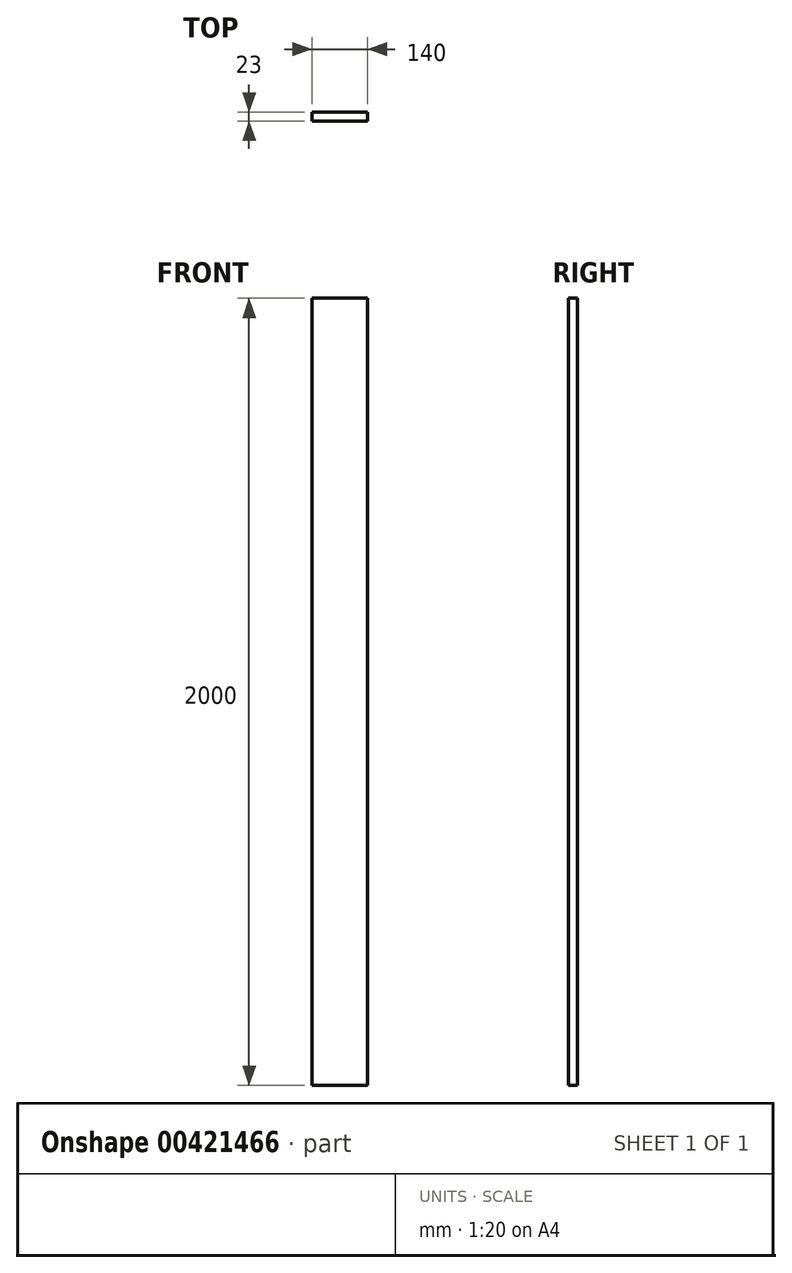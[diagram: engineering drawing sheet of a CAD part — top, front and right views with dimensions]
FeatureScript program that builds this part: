
annotation { "Feature Type Name" : "Feature", "Feature Type Description" : "" }
export const myFeature = defineFeature(function(context is Context, id is Id, definition is map)
    precondition{}
    {
        {
            var Q0;
            Q0=qCreatedBy(makeId("Front.planeOp"),FACE);
            var sketch = newSketch(context, id + "F0", { "sketchPlane" : qUnion([Q0])});
            skLineSegment(sketch, "E0.bottom", {"start": v(-149.18, -984.7) * mm, "end": v(-289.18, -984.7) * mm});
            skLineSegment(sketch, "E0.top", {"start": v(-149.18, 1015.3) * mm, "end": v(-289.18, 1015.3) * mm});
            skLineSegment(sketch, "E0.left", {"start": v(-149.18, -984.7) * mm, "end": v(-149.18, 1015.3) * mm});
            skLineSegment(sketch, "E0.right", {"start": v(-289.18, -984.7) * mm, "end": v(-289.18, 1015.3) * mm});
            skPoint(sketch, "E0.middle", {"position": v(-219.18, 15.3) * mm});
            skSolve(sketch);
        }
        {
            var Q0;
            Q0=makeQuery(id+"F0.imprint","IMPRINT",FACE,{"disambiguationData":[TD([[makeQuery(id+"F0.imprint","IMPRINT",EDGE,{"derivedFrom":sQuery(id+"F0.wireOp",EDGE,"E0.bottom")}),-1.0]])]});
            extrude(context, id + "F1", {"entities" : qUnion([Q0]), "depth" : 23 * mm});
        }
    });
